# Revit family: Hand_Shower_Hose-American_Standard-8888.035
name_source: partatom
category: Plumbing Fixtures
units: mm (PartAtom-declared; Revit-internal decimal feet)

## family parameters
Cut with Voids When Loaded = No
Host = Face
OmniClass Number = 23.45.05.14.17
OmniClass Title = Showers
Part Type = Normal
Room Calculation Point = No
Round Connector Dimension = Use Diameter
Shared = Yes

## types (6) — shared parameters
Assembly Code = D2010710
CW Connection = Yes
CWFU = 1
Cold Water Connection Diameter = 1/2"
Cold Water Connection Radius = 1/4"
Default Elevation = 44"
Description = Handshower Metal Shower Hose.Threads directly on 1/2" NPSM male threaded personal hand held shower.
HW Connection = Yes
HWFU = 2
Hot Water Connection Diameter = 1"
Hot Water Connection Radius = 1/4"
Installation Type = Wall-Mounted
Manufacturer = American Standard
Price = Prices may vary. Please consult Manufacturer Representative for most up-to-date price list.
Product Documentation Link = https://www.americanstandard.ca
Product Page URL = https://www.americanstandard.ca
URL = https://www.americanstandard-us.com
Vent Connection = No
WFU = 2
Warranty Information = Limited 1-Year Warranty
Waste Connection = No

## per-type parameters (varying)
| type | Finish | Height | Length | Material | Width |
| 8888.035.002 | Brass-American Standard-002-Polished Chrome | 23 5/8" | 0" | Brass-American Standard-002-Polished Chrome | 5" |
| 8888.035.295 | Brass-American Standard-295-Satin PVD | 23 5/8" | 0" | Brass-American Standard-295-Satin PVD | 5" |
| 8888.035.278 | Brass-American Standard-278-Legacy Bronze | 23 5/8" | 0" | Brass-American Standard-278-Legacy Bronze | 5" |
| 8888.035.243 | Brass-American Standard-243-Matte Black | 23 5/8" | 0" | Brass-American Standard-243-Matte Black | 5" |
| 8888.035.224 | Brass-American Standard-224-Oil Rubbed Bronze | 23 5/8" | 0" | Brass-American Standard-224-Oil Rubbed Bronze | 5" |
| 8888.035.013 | Brass-American Standard-013-Polished Nickel | 0" | 59" | Brass-American Standard-013-Polished Nickel | 0" |

note: column(s) folded — value = type name in every type: Model

## geometry (parser evidence)
native form markers: Sweep x3
no freeform markers — native parametric forms only
